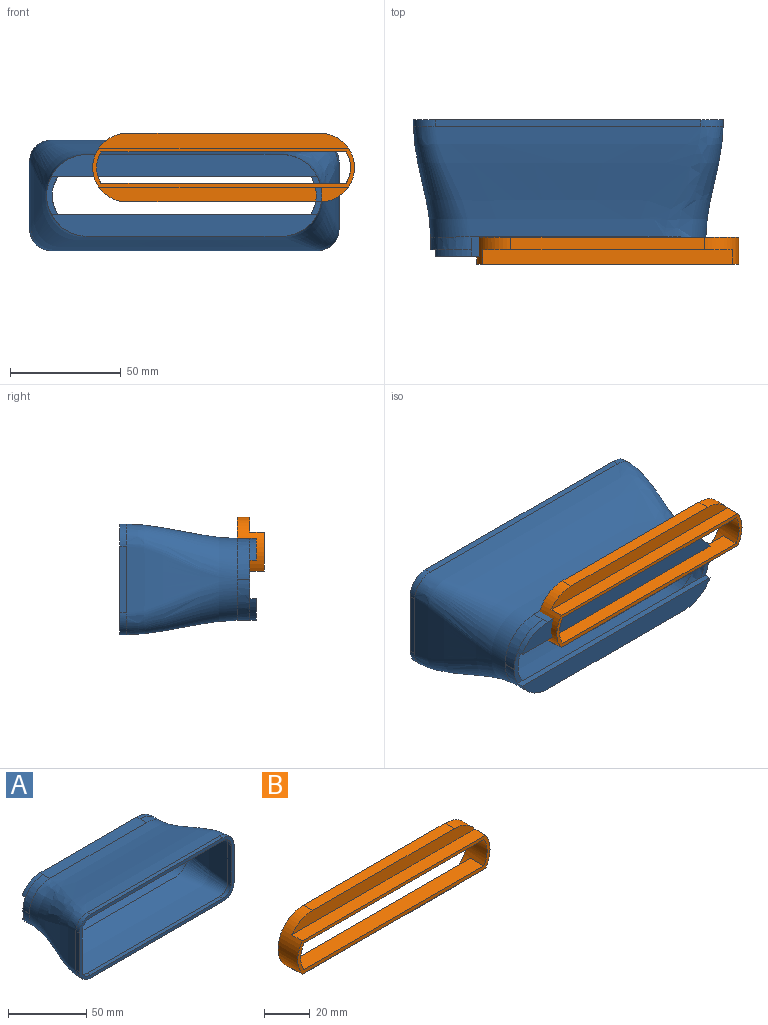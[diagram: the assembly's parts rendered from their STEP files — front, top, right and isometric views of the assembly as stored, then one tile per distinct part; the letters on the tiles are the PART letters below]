
ASSEMBLY  parts=2 mates=1
PART A: 49 faces, bbox 147.9x69.7x57.9 mm
  f0: plane 114.26x7.27mm, normal (0,-1,0), area 771.2mm2, adj f32,f33,f48
  f1: plane 5.81x0.11mm, normal (-1,0,0), area 0.6mm2, adj f15,f34,f35,f46
  f2: plane 5.81x0.11mm, normal (1,0,0), area 0.6mm2, adj f15,f37,f38,f45
  f3: extruded ~16.27x9.75mm, area 59.8mm2, adj f5,f35,f36,f48
  f4: extruded ~16.27x9.75mm, area 59.8mm2, adj f5,f36,f37,f48
  f5: plane 120.11x9.78mm, normal (0,1,0), area 1079.2mm2, adj f3,f4,f36,f48
  f6: cylinder r=10mm len=10mm, axis (0,1,0), area 47.1mm2, adj f7,f13,f14,f15
  f7: plane 120x3mm, normal (0,0,-1), area 360mm2, adj f6,f8,f14,f15
  f8: cylinder r=10mm len=10mm, axis (0,1,0), area 47.1mm2, adj f7,f9,f14,f15
  f9: plane 30x3mm, normal (1,0,0), area 90mm2, adj f8,f10,f14,f15
  f10: cylinder r=10mm len=10mm, axis (0,1,0), area 47.1mm2, adj f9,f11,f14,f15
  f11: plane 120x3mm, normal (0,0,1), area 360mm2, adj f10,f12,f14,f15
  f12: cylinder r=10mm len=10mm, axis (0,1,0), area 47.1mm2, adj f11,f13,f14,f15
  f13: plane 30x3mm, normal (-1,0,0), area 90mm2, adj f6,f12,f14,f15
  f14: plane 140x50mm, normal (0,-1,0), area 887.4mm2, adj f6,f7,f8,f9,f10,f11,f12,f13
  f15: bspline ~140x50mm, area 16651.1mm2, adj f1,f2,f6,f7,f8,f9,f10,f11
  f16: offset ~25.39x23.67mm, area 411.5mm2, adj f18,f19,f29,f33
  f17: bspline ~19.36x16.31mm, area 194.7mm2, adj f18,f20,f29,f31
  f18: offset ~118.12x23.73mm, area 2154.7mm2, adj f16,f17,f29,f32
  f19: bspline ~19.36x16.31mm, area 194.7mm2, adj f16,f20,f29,f40
  f20: offset ~133.01x23.73mm, area 2570.6mm2, adj f17,f19,f29,f30
  f21: cylinder r=7.5mm len=7.5mm, axis (0,1,0), area 35.3mm2, adj f14,f22,f28,f29
  f22: plane 127.89x10.89mm, normal (0,0,1), area 360mm2, adj f14,f21,f23,f29
  f23: cylinder r=7.5mm len=7.5mm, axis (0,1,0), area 35.3mm2, adj f14,f22,f24,f29
  f24: plane 33.01x6.01mm, normal (-1,0,0), area 90mm2, adj f14,f23,f25,f29
  f25: cylinder r=7.5mm len=7.5mm, axis (0,1,0), area 35.3mm2, adj f14,f24,f26,f29
  f26: plane 127.89x10.89mm, normal (0,0,-1), area 360mm2, adj f14,f25,f27,f29
  f27: cylinder r=7.5mm len=7.5mm, axis (0,1,0), area 35.3mm2, adj f14,f26,f28,f29
  f28: plane 33.01x6.01mm, normal (1,0,0), area 90mm2, adj f14,f21,f27,f29
  f29: offset ~145x55mm, area 10215.3mm2, adj f16,f17,f18,f19,f20,f21,f22,f23
  f30: extruded ~118.77x13.32mm, area 762.1mm2, adj f20,f31,f40,f41,f45,f46
  f31: extruded ~6.31x5.8mm, area 36.8mm2, adj f17,f30,f32,f45
  f32: extruded ~103.04x12.37mm, area 631.7mm2, adj f0,f18,f31,f33,f45
  f33: extruded ~15.73x13.32mm, area 130mm2, adj f0,f16,f32,f40,f46
  f34: extruded ~18.45x18.45mm, area 168.1mm2, adj f1,f15,f39,f42,f46
  f35: extruded ~18.45x18.45mm, area 168.1mm2, adj f1,f3,f15,f36,f46
  f36: plane 87.5x8.8mm, normal (0,0,1), area 770mm2, adj f3,f4,f5,f15,f35,f37
  f37: extruded ~18.45x18.45mm, area 168.1mm2, adj f2,f4,f15,f36,f45
  f38: extruded ~18.45x18.45mm, area 168.1mm2, adj f2,f15,f39,f43,f45
  f39: plane 87.5x8.8mm, normal (0,0,-1), area 770mm2, adj f15,f34,f38,f42,f43,f44
  f40: extruded ~6.31x5.8mm, area 36.8mm2, adj f19,f30,f33,f46
  f41: plane 114.24x7.25mm, normal (0,-1,0), area 771mm2, adj f30,f47
  f42: extruded ~16.27x9.75mm, area 59.8mm2, adj f34,f39,f44,f47
  f43: extruded ~16.27x9.75mm, area 59.8mm2, adj f38,f39,f44,f47
  f44: plane 120.11x9.78mm, normal (0,1,0), area 1079.1mm2, adj f39,f42,f43,f47
  f45: plane 17.6x5.18mm, normal (0,1,0), area 46mm2, adj f2,f30,f31,f32,f37,f38,f47,f48
  f46: plane 17.6x5.18mm, normal (0,1,0), area 45.8mm2, adj f1,f30,f33,f34,f35,f40,f47,f48
  f47: plane 120.04x3mm, normal (0,0,1), area 360.1mm2, adj f41,f42,f43,f44,f45,f46
  f48: plane 120.04x3mm, normal (0,0,-1), area 360.1mm2, adj f0,f3,f4,f5,f45,f46
PART B: 18 faces, bbox 118.4x12.2x31 mm
  f0: cylinder r=15.5mm len=31mm, axis (0,-1,0), area 400mm2, adj f1,f3,f4,f5,f6,f7,f8,f9
  f1: plane 87.4x5.7mm, normal (0,0,-1), area 498.2mm2, adj f0,f2,f5,f7
  f2: cylinder r=15.5mm len=31mm, axis (0,-1,0), area 400mm2, adj f1,f3,f4,f5,f6,f7,f8,f9
  f3: plane 87.4x5.7mm, normal (0,0,1), area 498.2mm2, adj f0,f2,f5,f9
  f4: plane 118.4x17.7mm, normal (0,-1,0), area 463.3mm2, adj f0,f2,f6,f8,f10,f12,f14,f16
  f5: plane 118.4x31mm, normal (0,1,0), area 479.8mm2, adj f0,f1,f2,f3,f10,f11,f12,f13
  f6: plane 112.85x6.5mm, normal (0,0,-1), area 733.5mm2, adj f0,f2,f4,f7
  f7: plane 112.85x6.65mm, normal (0,-1,0), area 700mm2, adj f0,f1,f2,f6
  f8: plane 112.85x6.5mm, normal (0,0,1), area 733.5mm2, adj f0,f2,f4,f9
  f9: plane 112.85x6.65mm, normal (0,-1,0), area 700mm2, adj f0,f2,f3,f8
  f10: cylinder r=13.7mm len=27.4mm, axis (0,-1,0), area 290.8mm2, adj f4,f5,f11,f13,f14,f15,f16,f17
  f11: plane 87.4x3.9mm, normal (0,0,1), area 340.9mm2, adj f5,f10,f12,f15
  f12: cylinder r=13.7mm len=27.4mm, axis (0,-1,0), area 290.8mm2, adj f4,f5,f11,f13,f14,f15,f16,f17
  f13: plane 87.4x3.9mm, normal (0,0,-1), area 340.9mm2, adj f5,f10,f12,f17
  f14: plane 110.89x8.3mm, normal (0,0,1), area 920.4mm2, adj f4,f10,f12,f15
  f15: plane 110.89x6.65mm, normal (0,1,0), area 691.8mm2, adj f10,f11,f12,f14
  f16: plane 110.89x8.3mm, normal (0,0,-1), area 920.4mm2, adj f4,f10,f12,f17
  f17: plane 110.89x6.65mm, normal (0,1,0), area 691.8mm2, adj f10,f12,f13,f16
PLACE A rot(axis=(0,0,-1),180deg) t=(113.63,-92.48,-2.54)mm
PLACE B t=(131.41,-98.28,10.05)mm
MATE planar B.f9 <-> A.f0  axis (0,-1,0) through (131.41,-98.28,22.12)mm
